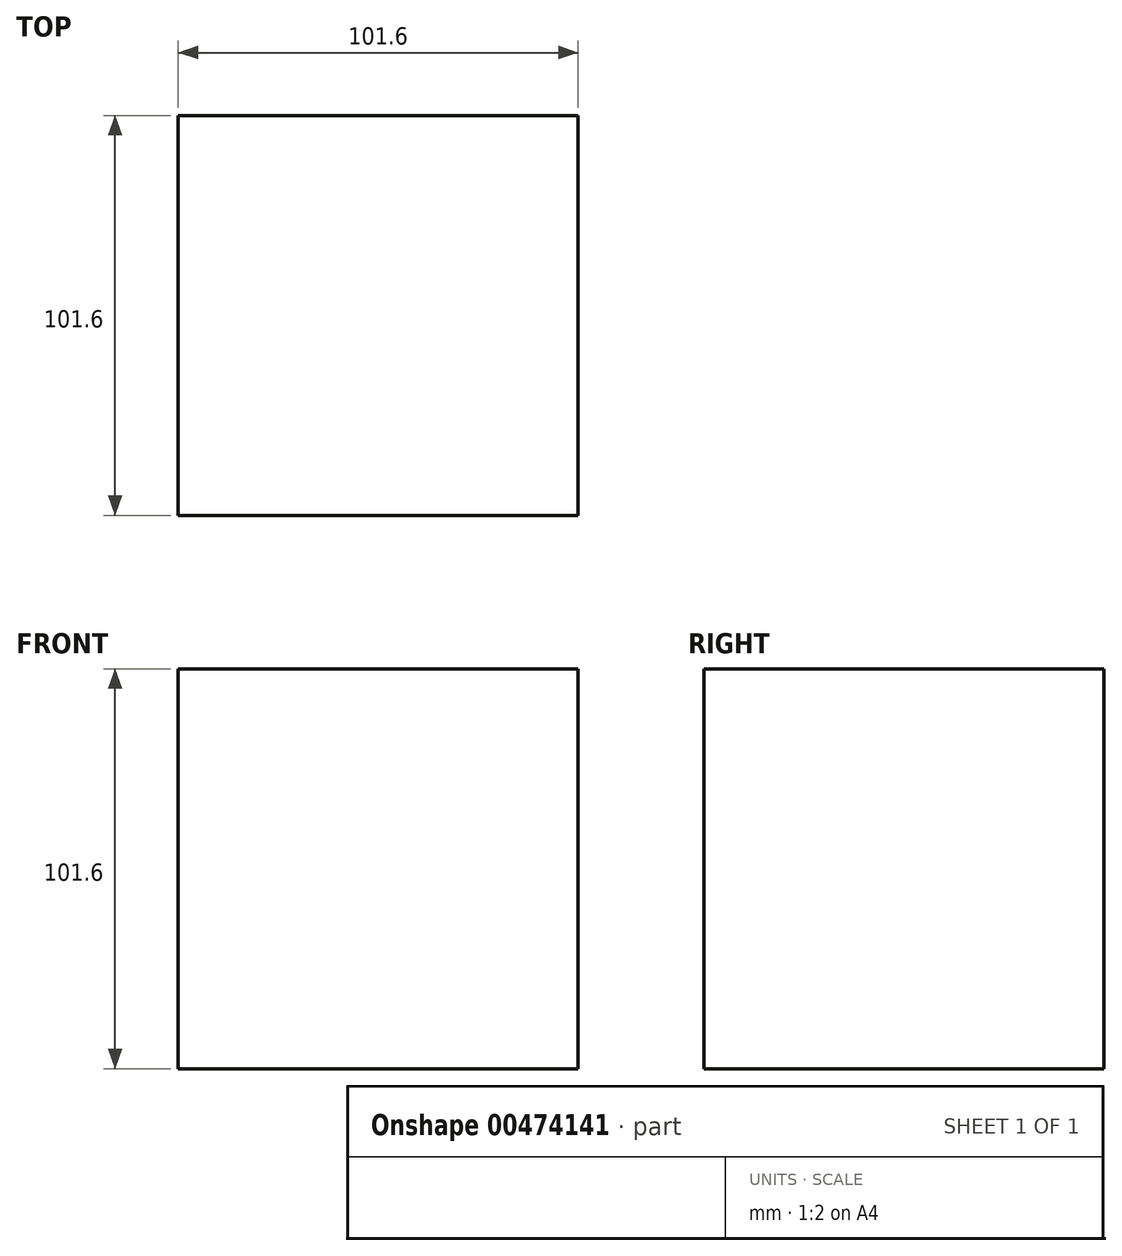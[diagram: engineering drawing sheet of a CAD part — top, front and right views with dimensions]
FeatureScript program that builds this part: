
annotation { "Feature Type Name" : "Feature", "Feature Type Description" : "" }
export const myFeature = defineFeature(function(context is Context, id is Id, definition is map)
    precondition{}
    {
        {
            var Q0;
            Q0=qCreatedBy(makeId("Front.planeOp"),FACE);
            var sketch = newSketch(context, id + "F0", { "sketchPlane" : qUnion([Q0])});
            skLineSegment(sketch, "E0", {"start": v(-50.8, 0) * mm, "end": v(50.8, 0) * mm});
            skLineSegment(sketch, "E1", {"start": v(50.8, 0) * mm, "end": v(50.8, -101.6) * mm});
            skLineSegment(sketch, "E2", {"start": v(50.8, -101.6) * mm, "end": v(-50.8, -101.6) * mm});
            skLineSegment(sketch, "E3", {"start": v(-50.8, -101.6) * mm, "end": v(-50.8, 0) * mm});
            skPoint(sketch, "E4", {"position": v(0, 0) * mm});
            skSolve(sketch);
        }
        {
            var Q0;
            Q0=makeQuery(id+"F0.imprint","IMPRINT",FACE,{"disambiguationData":[TD([[makeQuery(id+"F0.imprint","IMPRINT",EDGE,{"derivedFrom":sQuery(id+"F0.wireOp",EDGE,"E0")}),-1.0]])]});
            extrude(context, id + "F1", {"entities" : qUnion([Q0]), "depth" : 101.6 * mm});
        }
    });
